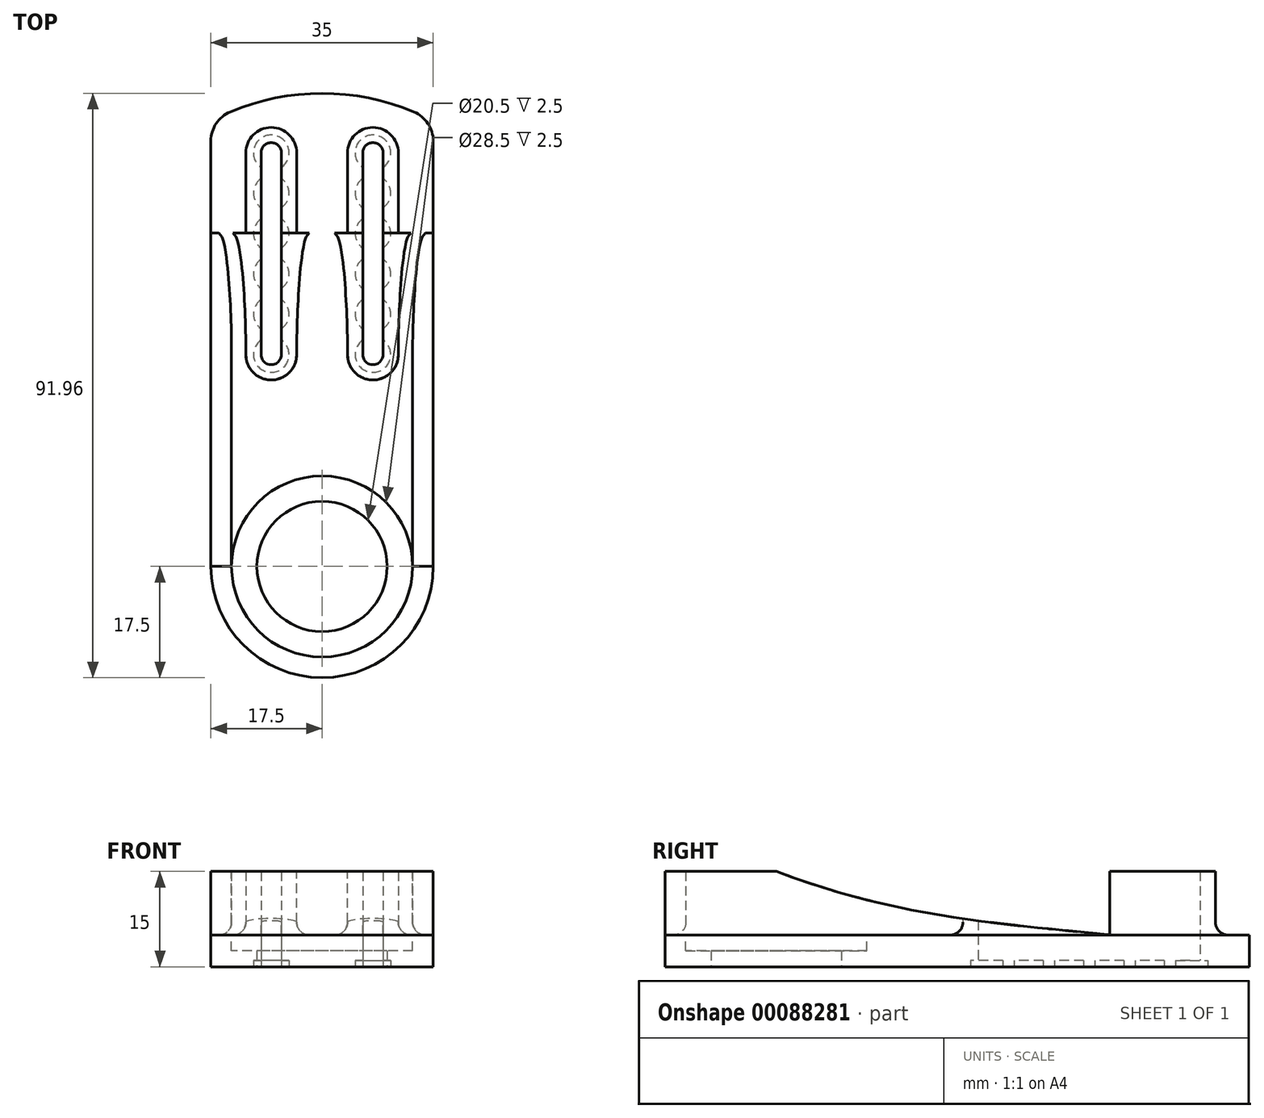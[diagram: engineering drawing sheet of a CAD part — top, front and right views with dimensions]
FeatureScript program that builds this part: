
annotation { "Feature Type Name" : "Feature", "Feature Type Description" : "" }
export const myFeature = defineFeature(function(context is Context, id is Id, definition is map)
    precondition{}
    {
        {
            var Q0;
            Q0=qCreatedBy(makeId("Top.planeOp"),FACE);
            var sketch = newSketch(context, id + "F0", { "sketchPlane" : qUnion([Q0])});
            skCircle(sketch, "E0", {"center": v(0, 0) * mm, "radius": 10.25 * mm});
            skCircle(sketch, "E1", {"center": v(0, 0) * mm, "radius": 39.7 * mm, "construction": true});
            skCircle(sketch, "E2", {"center": v(0, 0) * mm, "radius": 46.05 * mm, "construction": true});
            skCircle(sketch, "E3", {"center": v(0, 0) * mm, "radius": 52.4 * mm, "construction": true});
            skCircle(sketch, "E4", {"center": v(0, 0) * mm, "radius": 58.75 * mm, "construction": true});
            skCircle(sketch, "E5", {"center": v(0, 0) * mm, "radius": 65.1 * mm, "construction": true});
            skPoint(sketch, "E6.orphan", {"position": v(0, 60.75) * mm});
            skCircle(sketch, "E7", {"center": v(0, 0) * mm, "radius": 33.35 * mm, "construction": true});
            skArc(sketch, "E8", {"start": v(17.5, 0) * mm, "mid": v(0, -17.5) * mm, "end": v(-17.5, 0) * mm});
            skLineSegment(sketch, "E9", {"start": v(-17.5, 0) * mm, "end": v(-17.5, 70.1) * mm});
            skLineSegment(sketch, "E10", {"start": v(17.5, 0) * mm, "end": v(17.5, 70.1) * mm});
            skLineSegment(sketch, "E11", {"start": v(0, 0) * mm, "end": v(0, 72.3) * mm, "construction": true});
            skLineSegment(sketch, "E12", {"start": v(0, 33.35) * mm, "end": v(-8, 33.35) * mm, "construction": true});
            skArc(sketch, "E13", {"start": v(-9.6, 33.35) * mm, "mid": v(-8, 31.75) * mm, "end": v(-6.4, 33.35) * mm});
            skArc(sketch, "E14", {"start": v(-4, 33.35) * mm, "mid": v(-8, 29.35) * mm, "end": v(-12, 33.35) * mm});
            skLineSegment(sketch, "E15", {"start": v(0, 65.1) * mm, "end": v(-8, 65.1) * mm, "construction": true});
            skLineSegment(sketch, "E16", {"start": v(-6.4, 33.35) * mm, "end": v(-6.4, 65.1) * mm});
            skLineSegment(sketch, "E17", {"start": v(-9.6, 33.35) * mm, "end": v(-9.6, 65.1) * mm});
            skLineSegment(sketch, "E18", {"start": v(-12, 33.35) * mm, "end": v(-12, 65.1) * mm});
            skArc(sketch, "E19", {"start": v(-9.6, 65.1) * mm, "mid": v(-8, 66.7) * mm, "end": v(-6.4, 65.1) * mm});
            skArc(sketch, "E20", {"start": v(-12, 65.1) * mm, "mid": v(-8, 69.1) * mm, "end": v(-4, 65.1) * mm});
            skLineSegment(sketch, "E21", {"start": v(-4, 65.1) * mm, "end": v(-4, 33.35) * mm});
            skLineSegment(sketch, "E22.MirrorCS", {"start": v(4, 65.1) * mm, "end": v(4, 33.35) * mm});
            skLineSegment(sketch, "E23.MirrorCS", {"start": v(6.4, 33.35) * mm, "end": v(6.4, 65.1) * mm});
            skLineSegment(sketch, "E24.MirrorCS", {"start": v(9.6, 33.35) * mm, "end": v(9.6, 65.1) * mm});
            skLineSegment(sketch, "E25.MirrorCS", {"start": v(12, 33.35) * mm, "end": v(12, 65.1) * mm});
            skArc(sketch, "E26.MirrorCS", {"start": v(12, 65.1) * mm, "mid": v(8, 69.1) * mm, "end": v(4, 65.1) * mm});
            skArc(sketch, "E27.MirrorCS", {"start": v(9.6, 65.1) * mm, "mid": v(8, 66.7) * mm, "end": v(6.4, 65.1) * mm});
            skArc(sketch, "E28.MirrorCS", {"start": v(9.6, 33.35) * mm, "mid": v(8, 31.75) * mm, "end": v(6.4, 33.35) * mm});
            skArc(sketch, "E29.MirrorCS", {"start": v(4, 33.35) * mm, "mid": v(8, 29.35) * mm, "end": v(12, 33.35) * mm});
            skArc(sketch, "E30", {"start": v(17.5, 70.1) * mm, "mid": v(0, 74.46) * mm, "end": v(-17.5, 70.1) * mm});
            skLineSegment(sketch, "E31", {"start": v(0, 39.7) * mm, "end": v(-14.9, 39.7) * mm, "construction": true});
            skLineSegment(sketch, "E32", {"start": v(0, 46.05) * mm, "end": v(-14.23, 46.05) * mm, "construction": true});
            skLineSegment(sketch, "E33", {"start": v(0, 52.4) * mm, "end": v(-14.1, 52.4) * mm, "construction": true});
            skLineSegment(sketch, "E34", {"start": v(0, 58.75) * mm, "end": v(-14.12, 58.75) * mm, "construction": true});
            skLineSegment(sketch, "E35", {"start": v(-8, 65.1) * mm, "end": v(-8, 33.35) * mm, "construction": true});
            skSolve(sketch);
        }
        {
            var Q0;
            Q0=makeQuery(id+"F0.imprint","IMPRINT",FACE,{"disambiguationData":[TD([[makeQuery(id+"F0.imprint","IMPRINT",EDGE,{"derivedFrom":sQuery(id+"F0.wireOp",EDGE,"E0")}),-1.0]])]});
            var Q1;
            Q1=makeQuery(id+"F0.imprint","IMPRINT",FACE,{"disambiguationData":[TD([[makeQuery(id+"F0.imprint","IMPRINT",EDGE,{"derivedFrom":sQuery(id+"F0.wireOp",EDGE,"E13")}),-1.0]])]});
            var Q2;
            Q2=makeQuery(id+"F0.imprint","IMPRINT",FACE,{"disambiguationData":[TD([[makeQuery(id+"F0.imprint","IMPRINT",EDGE,{"derivedFrom":sQuery(id+"F0.wireOp",EDGE,"E22.MirrorCS")}),1.0]])]});
            extrude(context, id + "F1", {"entities" : qUnion([Q0, Q1, Q2]), "depth" : 5 * mm});
        }
        {
            var Q0;
            Q0=makeQuery(id+"F1.opExtrude","CAP_FACE",FACE,{"disambiguationData":[OSD([sQuery(id+"F0.wireOp",EDGE,"E0"),sQuery(id+"F0.wireOp",EDGE,"f8f96727-904b-4eb7-9f95-d02176fa3c95"),sQuery(id+"F0.wireOp",EDGE,"0bac2603-e9d6-4d6f-a74a-cf334d479195"),sQuery(id+"F0.wireOp",EDGE,"322fbd76-3777-4edb-a089-19f0f4cc46d8"),sQuery(id+"F0.wireOp",EDGE,"9f9b8ee6-f9d2-4211-bb25-9a8e97dd86f8"),sQuery(id+"F0.wireOp",EDGE,"97e6440b-47a1-49c7-80e9-257fa8547343"),sQuery(id+"F0.wireOp",EDGE,"1ab9314c-830e-4b4d-9e44-66489cad0943"),sQuery(id+"F0.wireOp",EDGE,"ae0a0e09-80f8-4296-84e4-8120a26b9033"),sQuery(id+"F0.wireOp",EDGE,"f3de2ac0-5251-4d12-b1f8-405bfaed9b6c"),sQuery(id+"F0.wireOp",EDGE,"rkeUwmxN-hcPE-Y1tt-fcP4-ARy1Lb9wExJl"),sQuery(id+"F0.wireOp",EDGE,"022pBsUc-yELQ-oBZ5-cmHP-pyOwi3QMTefE")])],"isStart":false});
            var sketch = newSketch(context, id + "F2", { "sketchPlane" : qUnion([Q0])});
            skCircle(sketch, "E36", {"center": v(0, 0) * mm, "radius": 14.25 * mm});
            skSolve(sketch);
        }
        {
            var Q0;
            Q0=makeQuery(id+"F2.imprint","IMPRINT",FACE,{"disambiguationData":[TD([[makeQuery(id+"F2.imprint","IMPRINT",EDGE,{"derivedFrom":sQuery(id+"F2.wireOp",EDGE,"E36")}),1.0]])]});
            extrude(context, id + "F3", {"entities" : qUnion([Q0]), "operationType" : NewBodyOperationType.REMOVE, "oppositeDirection" : true, "depth" : 2.5 * mm});
        }
        {
            var Q0;
            Q0=makeQuery(id+"F0.imprint","IMPRINT",FACE,{"disambiguationData":[TD([[makeQuery(id+"F0.imprint","IMPRINT",EDGE,{"derivedFrom":sQuery(id+"F0.wireOp",EDGE,"E13")}),-1.0]])]});
            var Q1;
            Q1=makeQuery(id+"F0.imprint","IMPRINT",FACE,{"disambiguationData":[TD([[makeQuery(id+"F0.imprint","IMPRINT",EDGE,{"derivedFrom":sQuery(id+"F0.wireOp",EDGE,"E22.MirrorCS")}),1.0]])]});
            extrude(context, id + "F4", {"entities" : qUnion([Q0, Q1]), "operationType" : NewBodyOperationType.ADD, "depth" : 15 * mm});
        }
        {
            var Q0;
            Q0=makeQuery(id+"F4.boolean.opBoolean","INTERSECT",EDGE,{"derivedFrom":[makeQuery(id+"F1.opExtrude","CAP_FACE",FACE,{"disambiguationData":[OSD([sQuery(id+"F0.wireOp",EDGE,"E0"),sQuery(id+"F0.wireOp",EDGE,"E8"),sQuery(id+"F0.wireOp",EDGE,"E9"),sQuery(id+"F0.wireOp",EDGE,"E10"),sQuery(id+"F0.wireOp",EDGE,"E13"),sQuery(id+"F0.wireOp",EDGE,"E16"),sQuery(id+"F0.wireOp",EDGE,"E17"),sQuery(id+"F0.wireOp",EDGE,"E19"),sQuery(id+"F0.wireOp",EDGE,"E23.MirrorCS"),sQuery(id+"F0.wireOp",EDGE,"E24.MirrorCS"),sQuery(id+"F0.wireOp",EDGE,"E27.MirrorCS"),sQuery(id+"F0.wireOp",EDGE,"E28.MirrorCS"),sQuery(id+"F0.wireOp",EDGE,"E30")])],"isStart":false}),makeQuery(id+"F4.opExtrude","SWEPT_FACE",FACE,{"disambiguationData":[OSD([sQuery(id+"F0.wireOp",EDGE,"E18")])]})]});
            var Q1;
            Q1=makeQuery(id+"F4.boolean.opBoolean","INTERSECT",EDGE,{"derivedFrom":[makeQuery(id+"F1.opExtrude","CAP_FACE",FACE,{"disambiguationData":[OSD([sQuery(id+"F0.wireOp",EDGE,"E0"),sQuery(id+"F0.wireOp",EDGE,"E8"),sQuery(id+"F0.wireOp",EDGE,"E9"),sQuery(id+"F0.wireOp",EDGE,"E10"),sQuery(id+"F0.wireOp",EDGE,"E13"),sQuery(id+"F0.wireOp",EDGE,"E16"),sQuery(id+"F0.wireOp",EDGE,"E17"),sQuery(id+"F0.wireOp",EDGE,"E19"),sQuery(id+"F0.wireOp",EDGE,"E23.MirrorCS"),sQuery(id+"F0.wireOp",EDGE,"E24.MirrorCS"),sQuery(id+"F0.wireOp",EDGE,"E27.MirrorCS"),sQuery(id+"F0.wireOp",EDGE,"E28.MirrorCS"),sQuery(id+"F0.wireOp",EDGE,"E30")])],"isStart":false}),makeQuery(id+"F4.opExtrude","SWEPT_FACE",FACE,{"disambiguationData":[OSD([sQuery(id+"F0.wireOp",EDGE,"E22.MirrorCS")])]})]});
            fillet(context, id + "F5", {"entities" : qUnion([Q0, Q1]), "radius" : 2 * mm, "tangentPropagation" : true, "allowEdgeOverflow" : false});
        }
        {
            var Q0;
            Q0=makeQuery(id+"F1.opExtrude","SWEPT_EDGE",EDGE,{"disambiguationData":[OSD([sQuery(id+"F0.wireOp",EDGE,"E9"),sQuery(id+"F0.wireOp",EDGE,"E30")])]});
            var Q1;
            Q1=makeQuery(id+"F1.opExtrude","SWEPT_EDGE",EDGE,{"disambiguationData":[OSD([sQuery(id+"F0.wireOp",EDGE,"E10"),sQuery(id+"F0.wireOp",EDGE,"E30")])]});
            fillet(context, id + "F6", {"entities" : qUnion([Q0, Q1]), "radius" : 5 * mm, "tangentPropagation" : true, "allowEdgeOverflow" : false});
        }
        {
            var Q0;
            Q0=makeQuery(id+"F1.opExtrude","CAP_FACE",FACE,{"disambiguationData":[OSD([sQuery(id+"F0.wireOp",EDGE,"E0"),sQuery(id+"F0.wireOp",EDGE,"E8"),sQuery(id+"F0.wireOp",EDGE,"E9"),sQuery(id+"F0.wireOp",EDGE,"E10"),sQuery(id+"F0.wireOp",EDGE,"E13"),sQuery(id+"F0.wireOp",EDGE,"E16"),sQuery(id+"F0.wireOp",EDGE,"E17"),sQuery(id+"F0.wireOp",EDGE,"E19"),sQuery(id+"F0.wireOp",EDGE,"E23.MirrorCS"),sQuery(id+"F0.wireOp",EDGE,"E24.MirrorCS"),sQuery(id+"F0.wireOp",EDGE,"E27.MirrorCS"),sQuery(id+"F0.wireOp",EDGE,"E28.MirrorCS"),sQuery(id+"F0.wireOp",EDGE,"E30")])],"isStart":true});
            var sketch = newSketch(context, id + "F7", { "sketchPlane" : qUnion([Q0])});
            skCircle(sketch, "E37", {"center": v(-8, -65.1) * mm, "radius": 2.8 * mm});
            skCircle(sketch, "E38.0.1.0", {"center": v(-8, -58.75) * mm, "radius": 2.8 * mm});
            skCircle(sketch, "E38.0.2.0", {"center": v(-8, -52.4) * mm, "radius": 2.8 * mm});
            skCircle(sketch, "E38.0.3.0", {"center": v(-8, -46.05) * mm, "radius": 2.8 * mm});
            skCircle(sketch, "E38.0.4.0", {"center": v(-8, -39.7) * mm, "radius": 2.8 * mm});
            skCircle(sketch, "E38.0.5.0", {"center": v(-8, -33.35) * mm, "radius": 2.8 * mm});
            skCircle(sketch, "E38.1.0.0", {"center": v(8, -65.1) * mm, "radius": 2.8 * mm});
            skCircle(sketch, "E38.1.1.0", {"center": v(8, -58.75) * mm, "radius": 2.8 * mm});
            skCircle(sketch, "E38.1.2.0", {"center": v(8, -52.4) * mm, "radius": 2.8 * mm});
            skCircle(sketch, "E38.1.3.0", {"center": v(8, -46.05) * mm, "radius": 2.8 * mm});
            skCircle(sketch, "E38.1.4.0", {"center": v(8, -39.7) * mm, "radius": 2.8 * mm});
            skCircle(sketch, "E38.1.5.0", {"center": v(8, -33.35) * mm, "radius": 2.8 * mm});
            skLineSegment(sketch, "E38.direction1", {"start": v(-8, -65.1) * mm, "end": v(8, -65.1) * mm, "construction": true});
            skLineSegment(sketch, "E38.direction2", {"start": v(-8, -65.1) * mm, "end": v(-8, -58.75) * mm, "construction": true});
            skSolve(sketch);
        }
        {
            var Q0;
            Q0 = qSketchRegion(id + "F7", true);
            extrude(context, id + "F8", {"entities" : qUnion([Q0]), "operationType" : NewBodyOperationType.REMOVE, "oppositeDirection" : true, "depth" : 1 * mm});
        }
        {
            var Q0;
            Q0=makeQuery(id+"F1.opExtrude","CAP_FACE",FACE,{"disambiguationData":[OSD([sQuery(id+"F0.wireOp",EDGE,"E0"),sQuery(id+"F0.wireOp",EDGE,"E8"),sQuery(id+"F0.wireOp",EDGE,"E9"),sQuery(id+"F0.wireOp",EDGE,"E10"),sQuery(id+"F0.wireOp",EDGE,"E13"),sQuery(id+"F0.wireOp",EDGE,"E16"),sQuery(id+"F0.wireOp",EDGE,"E17"),sQuery(id+"F0.wireOp",EDGE,"E19"),sQuery(id+"F0.wireOp",EDGE,"E23.MirrorCS"),sQuery(id+"F0.wireOp",EDGE,"E24.MirrorCS"),sQuery(id+"F0.wireOp",EDGE,"E27.MirrorCS"),sQuery(id+"F0.wireOp",EDGE,"E28.MirrorCS"),sQuery(id+"F0.wireOp",EDGE,"E30")])],"isStart":false});
            var sketch = newSketch(context, id + "F9", { "sketchPlane" : qUnion([Q0])});
            skLineSegment(sketch, "E39", {"start": v(-17.5, 52.48) * mm, "end": v(17.5, 52.48) * mm});
            skLineSegment(sketch, "E40", {"start": v(14.25, 0) * mm, "end": v(14.25, 52.48) * mm});
            skLineSegment(sketch, "E41", {"start": v(-14.25, 0) * mm, "end": v(-14.25, 52.48) * mm});
            skSolve(sketch);
        }
        {
            var Q0;
            {var subQ0=sQuery(id+"F9.wireOp",EDGE,"E40");Q0=makeQuery(id+"F9.imprint","IMPRINT",FACE,{"disambiguationData":[TD([[makeQuery(id+"F9.imprint","IMPRINT",EDGE,{"derivedFrom":subQ0}),-1.0]])]});}
            extrude(context, id + "F10", {"entities" : qUnion([Q0]), "depth" : 10 * mm});
        }
        {
            var Q0;
            Q0=makeQuery(id+"F10.opExtrude","SWEPT_FACE",FACE,{"disambiguationData":[OSD([sQuery(id+"F0.wireOp",EDGE,"E9")])]});
            var sketch = newSketch(context, id + "F11", { "sketchPlane" : qUnion([Q0])});
            skFitSpline(sketch, "E42", {"points": [v(-52.48, 5) * mm, v(0, 15) * mm], "startDerivative": vector(53.65, 5.63) * mm, "endDerivative": vector(57.98, 21.87) * mm});
            skSolve(sketch);
        }
        {
            var Q0;
            Q0=makeQuery(id+"F11.imprint","IMPRINT",FACE,{"disambiguationData":[TD([[makeQuery(id+"F11.imprint","IMPRINT",EDGE,{"derivedFrom":sQuery(id+"F11.wireOp",EDGE,"E42")}),1.0]])]});
            extrude(context, id + "F12", {"entities" : qUnion([Q0]), "operationType" : NewBodyOperationType.REMOVE, "endBound" : BoundingType.THROUGH_ALL, "oppositeDirection" : true, "depth" : 25 * mm});
        }
        {
            var Q0;
            Q0=makeQuery(id+"F10.opExtrude","CAP_EDGE",EDGE,{"disambiguationData":[OSD([sQuery(id+"F9.wireOp",EDGE,"E40")])],"isStart":true});
            var Q1;
            Q1=makeQuery(id+"F10.opExtrude","CAP_EDGE",EDGE,{"disambiguationData":[OSD([sQuery(id+"F9.wireOp",EDGE,"E41")])],"isStart":true});
            fillet(context, id + "F13", {"entities" : qUnion([Q0, Q1]), "radius" : 2 * mm, "tangentPropagation" : true, "allowEdgeOverflow" : false});
        }
    });
